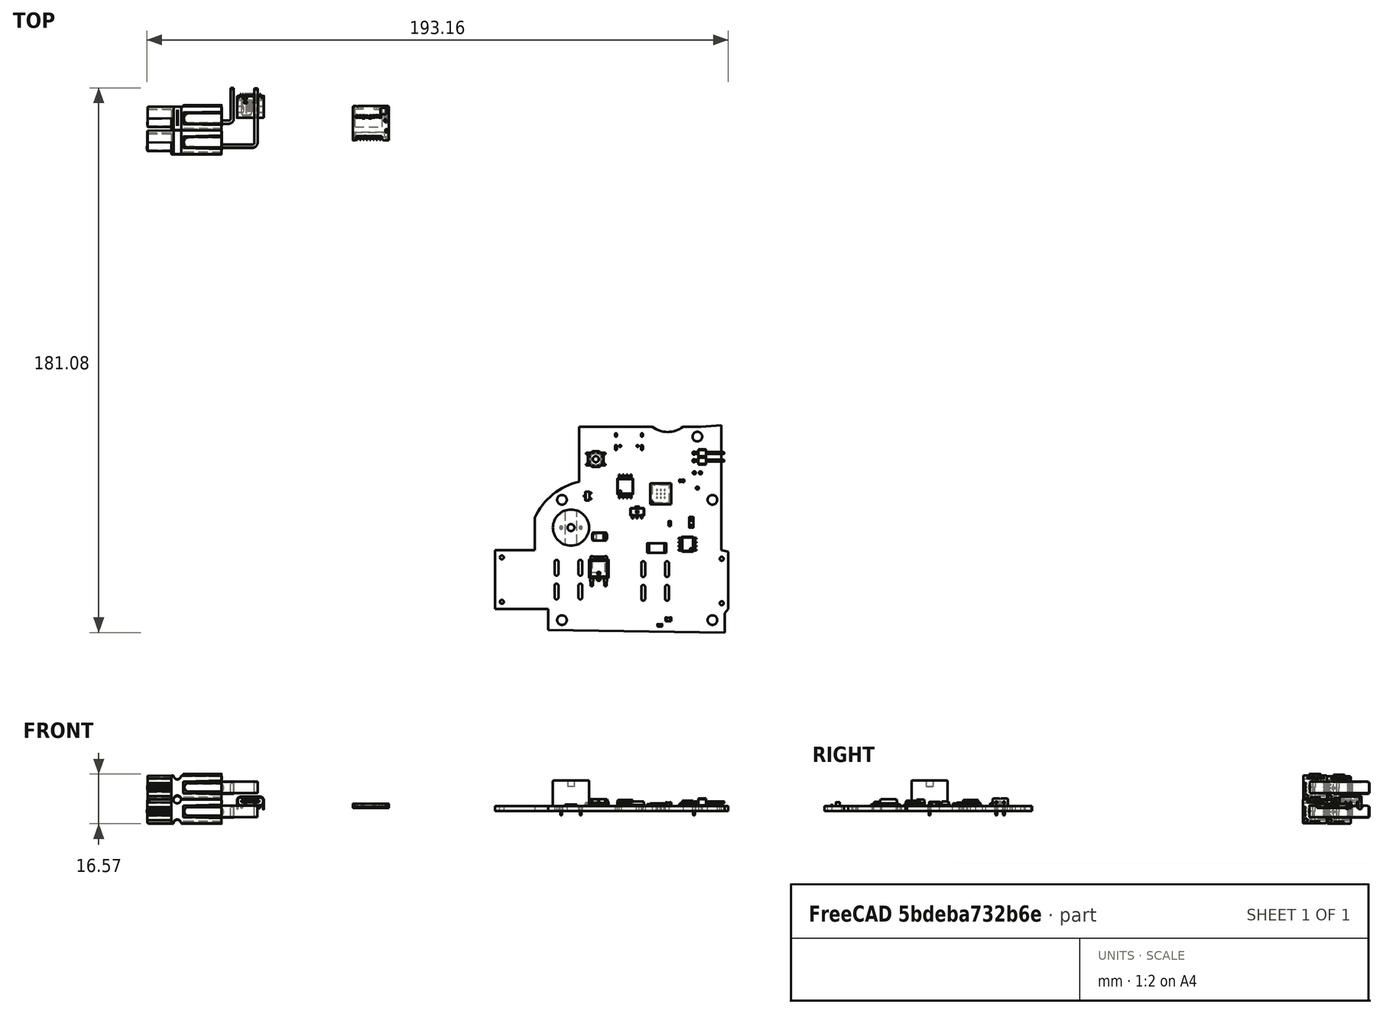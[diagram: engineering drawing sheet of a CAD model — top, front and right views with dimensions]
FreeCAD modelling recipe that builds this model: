
FCSTD DOCUMENT  (FreeCAD 0.20R27537 (Git))
Label: board
License: All rights reserved
LicenseURL: http://en.wikipedia.org/wiki/All_rights_reserved
objects: App::Link×56, Part::Feature×38, App::Part×8, PartDesign::CoordinateSystem×1, Sketcher::SketchObject×1
note: 40 computed .brp shape members not serialized (recipe doc carries the construction recipe); baked Part::Feature solids carry a one-line shape summary decoded from their .brp

FEATURE [PartDesign::CoordinateSystem] Local_CS_a133
  AttacherType = Attacher::AttachEngine3D
FEATURE [Part::Feature] Pcb_a133
  shape: bbox 77.5 x 68.95 x 1.6 mm, 118 faces (baked)
FEATURE [Sketcher::SketchObject] PCB_Sketch_a133
  ExternalGeometry = -> [Pcb_a133]
  FullyConstrained = false
  sketch-geometry (42):
    g0: ArcOfCircle CenterX=143.125 CenterY=-95.9167 CenterZ=0 NormalX=0 NormalY=0 NormalZ=-1 AngleXU=-2.2143 Radius=8.54167 StartAngle=0 EndAngle=1.287
    g1: LineSegment StartX=100.518 StartY=-132.657 StartZ=0 EndX=100.518 EndY=-140.91 EndZ=0
    g2: LineSegment StartX=97.2675 StartY=-144.16 StartZ=0 EndX=89.2675 EndY=-144.16 EndZ=0
    g3: LineSegment StartX=86.0175 StartY=-147.41 StartZ=0 EndX=86.0175 EndY=-159.69 EndZ=0
    g4: LineSegment StartX=89.2675 StartY=-162.94 StartZ=0 EndX=100.75 EndY=-162.94 EndZ=0
    g5: LineSegment StartX=104 StartY=-166.19 StartZ=0 EndX=104 EndY=-167.75 EndZ=0
    g6: LineSegment StartX=107.25 StartY=-171 StartZ=0 EndX=159.85 EndY=-171 EndZ=0
    g7: LineSegment StartX=163.1 StartY=-167.75 StartZ=0 EndX=163.1 EndY=-166.75 EndZ=0
    g8: LineSegment StartX=163.1 StartY=-166.75 StartZ=0 EndX=163.1 EndY=-146.61 EndZ=0
    g9: LineSegment StartX=161.1 StartY=-144.61 StartZ=0 EndX=160.25 EndY=-144.61 EndZ=0
    g10: LineSegment StartX=157 StartY=-141.36 StartZ=0 EndX=157 EndY=-132 EndZ=0
    g11: ArcOfCircle CenterX=158 CenterY=-127 CenterZ=0 NormalX=0 NormalY=0 NormalZ=1 AngleXU=0 Radius=4 StartAngle=4.71239 EndAngle=7.85398
    g12: LineSegment StartX=157 StartY=-122 StartZ=0 EndX=157 EndY=-106 EndZ=0
    g13: LineSegment StartX=153.75 StartY=-102.75 StartZ=0 EndX=148.25 EndY=-102.75 EndZ=0
    g14: LineSegment StartX=138 StartY=-102.75 StartZ=0 EndX=116.25 EndY=-102.75 EndZ=0
    g15: LineSegment StartX=113 StartY=-106 StartZ=0 EndX=113 EndY=-117.5 EndZ=0
    g16: ArcOfCircle CenterX=112.711 CenterY=-132.657 CenterZ=0 NormalX=0 NormalY=0 NormalZ=1 AngleXU=0 Radius=12.1931 StartAngle=1.7637 EndAngle=3.14159
    g17: GeomPoint X=106.689 Y=-126.083 Z=0
    g18: GeomPoint X=102.635 Y=-125.79 Z=0
    g19: ArcOfCircle CenterX=158 CenterY=-132 CenterZ=0 NormalX=0 NormalY=0 NormalZ=1 AngleXU=0 Radius=1 StartAngle=1.5708 EndAngle=3.14159
    g20: ArcOfCircle CenterX=160.25 CenterY=-141.36 CenterZ=0 NormalX=0 NormalY=0 NormalZ=1 AngleXU=0 Radius=3.25 StartAngle=3.14159 EndAngle=4.71239
    g21: GeomPoint X=157 Y=-144.61 Z=0
    g22: ArcOfCircle CenterX=161.1 CenterY=-146.61 CenterZ=0 NormalX=0 NormalY=0 NormalZ=1 AngleXU=0 Radius=2 StartAngle=-2.7e-15 EndAngle=1.5708
    g23: GeomPoint X=163.1 Y=-144.61 Z=0
    g24: ArcOfCircle CenterX=158 CenterY=-122 CenterZ=0 NormalX=0 NormalY=0 NormalZ=1 AngleXU=0 Radius=1 StartAngle=3.14159 EndAngle=4.71239
    g25: ArcOfCircle CenterX=153.75 CenterY=-106 CenterZ=0 NormalX=0 NormalY=0 NormalZ=1 AngleXU=0 Radius=3.25 StartAngle=1.3e-15 EndAngle=1.5708
    g26: GeomPoint X=157 Y=-102.75 Z=0
    g27: ArcOfCircle CenterX=116.25 CenterY=-106 CenterZ=0 NormalX=0 NormalY=0 NormalZ=1 AngleXU=0 Radius=3.25 StartAngle=1.5708 EndAngle=3.14159
    g28: GeomPoint X=113 Y=-102.75 Z=0
    g29: ArcOfCircle CenterX=109.75 CenterY=-117.5 CenterZ=0 NormalX=0 NormalY=0 NormalZ=1 AngleXU=0 Radius=3.25 StartAngle=4.90529 EndAngle=6.28319
    g30: ArcOfCircle CenterX=97.2675 CenterY=-140.91 CenterZ=0 NormalX=0 NormalY=0 NormalZ=1 AngleXU=0 Radius=3.25 StartAngle=4.71239 EndAngle=6.28319
    g31: GeomPoint X=100.518 Y=-144.16 Z=0
    g32: ArcOfCircle CenterX=89.2675 CenterY=-147.41 CenterZ=0 NormalX=0 NormalY=0 NormalZ=1 AngleXU=0 Radius=3.25 StartAngle=1.5708 EndAngle=3.14159
    g33: GeomPoint X=86.0175 Y=-144.16 Z=0
    g34: ArcOfCircle CenterX=89.2675 CenterY=-159.69 CenterZ=0 NormalX=0 NormalY=0 NormalZ=1 AngleXU=0 Radius=3.25 StartAngle=3.14159 EndAngle=4.71239
    g35: GeomPoint X=86.0175 Y=-162.94 Z=0
    g36: ArcOfCircle CenterX=100.75 CenterY=-166.19 CenterZ=0 NormalX=0 NormalY=0 NormalZ=1 AngleXU=0 Radius=3.25 StartAngle=-2.7e-15 EndAngle=1.5708
    g37: GeomPoint X=104 Y=-162.94 Z=0
    g38: ArcOfCircle CenterX=107.25 CenterY=-167.75 CenterZ=0 NormalX=0 NormalY=0 NormalZ=1 AngleXU=0 Radius=3.25 StartAngle=3.14159 EndAngle=4.71239
    g39: GeomPoint X=104 Y=-171 Z=0
    g40: ArcOfCircle CenterX=159.85 CenterY=-167.75 CenterZ=0 NormalX=0 NormalY=0 NormalZ=1 AngleXU=0 Radius=3.25 StartAngle=4.71239 EndAngle=6.28319
    g41: GeomPoint X=163.1 Y=-171 Z=0
  constraints (102):
    c: DistanceX(g-6,g-5) = 50
    c: DistanceX(g-3,g-4) = 50
    c: DistanceY(g-4,g-5) = 40
    c: DistanceY(g-3,g-6) = 40
    c: DistanceY(g-5,g-7) = 21
    c: DistanceX(g-7,g-5) = 5
    c: Horizontal(g2)
    c: Vertical(g3)
    c: Horizontal(g4)
    c: Vertical(g5)
    c: Horizontal(g6)
    c: Vertical(g7)
    c: Vertical(g8)
    c: Horizontal(g9)
    c: Vertical(g10)
    c: Coincident(g11,g-5)
    c: Coincident(g13,g0)
    c: Coincident(g14,g0)
    c: Horizontal(g14)
    c: Vertical(g15)
    c: Coincident(g16,g1)
    c: Vertical(g12)
    c: Horizontal(g13)
    c: Equal(g0,g-12)
    c: Coincident(g0,g-12)
    c: Coincident(g0,g-12)
    c: DistanceX(g-7,g26) = 4
    c: DistanceX(g-8,g23) = 2
    c: DistanceX(g33,g-10) = 2
    c: DistanceX(g39,g-3) = 4
    c: DistanceY(g39,g-3) = 4
    c: DistanceY(g-8,g23) = 2
    c: DistanceY(g35,g-11) = 2
    c: DistanceY(g-10,g33) = 2
    c: DistanceX(g28,g14) = 25
    c: PointOnObject(g17,g-6)
    c: PointOnObject(g18,g16)
    c: Distance(g-6,g18) = 5.5
    c: Tangent(g11,g19) = 1.5708
    c: Tangent(g10,g19) = 1.5708
    c: PointOnObject(g21,g10)
    c: PointOnObject(g21,g9)
    c: Tangent(g10,g20) = 1.5708
    c: Tangent(g9,g20) = 1.5708
    c: PointOnObject(g23,g9)
    c: PointOnObject(g23,g8)
    c: Tangent(g9,g22) = -1.5708
    c: Tangent(g8,g22) = -1.5708
    c: Tangent(g11,g24) = 1.5708
    c: Tangent(g12,g24) = 1.5708
    c: PointOnObject(g26,g12)
    c: PointOnObject(g26,g13)
    c: Tangent(g12,g25) = -1.5708
    c: Tangent(g13,g25) = -1.5708
    c: PointOnObject(g28,g14)
    c: PointOnObject(g28,g15)
    c: Tangent(g14,g27) = -1.5708
    c: Tangent(g15,g27) = -1.5708
    c: Tangent(g16,g29) = 1.5708
    c: Tangent(g15,g29) = 1.5708
    c: PointOnObject(g31,g2)
    c: PointOnObject(g31,g1)
    c: Tangent(g2,g30) = 1.5708
    c: Tangent(g1,g30) = 1.5708
    c: PointOnObject(g33,g3)
    c: PointOnObject(g33,g2)
    c: Tangent(g3,g32) = -1.5708
    c: Tangent(g2,g32) = -1.5708
    c: PointOnObject(g35,g3)
    c: PointOnObject(g35,g4)
    c: Tangent(g3,g34) = -1.5708
    c: Tangent(g4,g34) = -1.5708
    c: PointOnObject(g37,g5)
    c: PointOnObject(g37,g4)
    c: Tangent(g5,g36) = 1.5708
    c: Tangent(g4,g36) = 1.5708
    c: PointOnObject(g39,g5)
    c: PointOnObject(g39,g6)
    c: Tangent(g5,g38) = -1.5708
    c: Tangent(g6,g38) = -1.5708
    c: PointOnObject(g41,g6)
    c: PointOnObject(g41,g7)
    c: Tangent(g6,g40) = -1.5708
    c: Tangent(g7,g40) = -1.5708
    c: Coincident(g7,g8)
    c: Equal(g40,g38)
    c: Equal(g36,g34)
    c: Equal(g32,g34)
    c: Equal(g30,g32)
    c: Equal(g30,g20)
    c: Equal(g19,g24)
    c: Equal(g25,g27)
    c: Equal(g27,g29)
    c: Equal(g27,g30)
    c: Equal(g40,g25)
    c: Vertical(g10,g12)
    c: Radius(g11) = 4
    c: Vertical(g11,g24)
    c: Horizontal(g22,g-8)
    c: DistanceY(g7,g7) = 1
    c: DistanceY(g15,g15) = 11.5
    c: Block(g1)
FEATURE [App::Part] Board_Geoms_a133
  Group = -> [Local_CS_a133,Pcb_a133,PCB_Sketch_a133]
  Origin = -> Origin
FEATURE [Part::Feature] Shape  label="C11_C_0603_1608Metric_b2591ca4353f"
  Placement = pos=(147.8,-120.7,0) rot=(0,0,1;0rad)
  shape: bbox 1.6 x 0.8 x 0.8 mm, 28 faces (baked)
FEATURE [Part::Feature] Shape001  label="U4_SOIC_8_39x49mm_P127mm_40db203ede0f"
  Placement = pos=(149.75,-141.75,0) rot=(0,0,1;3.14159rad)
  shape: bbox 6 x 4.9 x 1.75 mm, 156 faces (baked)
FEATURE [Part::Feature] Shape002  label="R11_R_0603_1608Metric_8d44d50ded66"
  Placement = pos=(140.5,-168.75,0) rot=(0,0,1;3.14159rad)
  shape: bbox 1.6 x 0.8 x 0.45 mm, 26 faces (baked)
FEATURE [App::Link] C11_C_0603_1608Metric_b2591ca4353f_ln_  label="C1_C_0603_1608Metric_4f53b00ce3c0"
  LinkPlacement = pos=(132.368,-165.3,0) rot=(0,0,-1;1.5708rad)
  LinkedObject = -> Shape
  Placement = pos=(132.368,-165.3,0) rot=(0,0,-1;1.5708rad)
FEATURE [App::Link] C11_C_0603_1608Metric_b2591ca4353f_ln_001  label="C22_C_0603_1608Metric_e7c7fc5a71bd"
  LinkPlacement = pos=(138,-131.31,0) rot=(0,0,-1;1.5708rad)
  LinkedObject = -> Shape
  Placement = pos=(138,-131.31,0) rot=(0,0,-1;1.5708rad)
FEATURE [App::Link] R11_R_0603_1608Metric_8d44d50ded66_ln_  label="R18_R_0603_1608Metric_e3e5b9e3ae07"
  LinkPlacement = pos=(134.5,-122.35,0) rot=(0,0,1;3.14159rad)
  LinkedObject = -> Shape002
  Placement = pos=(134.5,-122.35,0) rot=(0,0,1;3.14159rad)
FEATURE [Part::Feature] Shape003  label="U2_SOT_89_3_d67087812165"
  Placement = pos=(133,-131.25,0) rot=(0,0,1;1.5708rad)
  shape: bbox 4.5 x 4 x 1.52 mm, 43 faces (baked)
FEATURE [App::Link] R11_R_0603_1608Metric_8d44d50ded66_ln_001  label="R29_R_0603_1608Metric_036824cd240c"
  LinkPlacement = pos=(148.25,-136.25,0) rot=(0,0,1;0rad)
  LinkedObject = -> Shape002
  Placement = pos=(148.25,-136.25,0) rot=(0,0,1;0rad)
FEATURE [App::Link] R11_R_0603_1608Metric_8d44d50ded66_ln_002  label="R15_R_0603_1608Metric_e011a92e6b2f"
  LinkPlacement = pos=(150,-117,0) rot=(0,0,1;1.5708rad)
  LinkedObject = -> Shape002
  Placement = pos=(150,-117,0) rot=(0,0,1;1.5708rad)
FEATURE [Part::Feature] Part__Feature  label="ConPins"
  shape: bbox 6 x 4.32 x 0.61 mm, 70 faces (baked)
FEATURE [Part::Feature] Part__Feature001  label="PcbPins"
  shape: bbox 6.9 x 0.99 x 0.3 mm, 122 faces (baked)
FEATURE [Part::Feature] Part__Feature002  label="Mold"
  shape: bbox 8.95 x 6.5 x 3.731 mm, 55 faces (baked)
FEATURE [Part::Feature] Part__Feature003  label="Frame"
  shape: bbox 8.95 x 7.3 x 4.2 mm, 323 faces (baked)
FEATURE [App::Part] HRO_TYPE_C_31_M_12  label="J5_HRO_TYPE_C_31_M_12_ee36a14f041e"
  Group = -> [Part__Feature,Part__Feature001,Part__Feature002,Part__Feature003]
  Origin = -> Origin008
  Placement = pos=(134.75,-103,0) rot=(0,0,1;3.14159rad)
FEATURE [App::Link] C11_C_0603_1608Metric_b2591ca4353f_ln_002  label="C14_C_0603_1608Metric_768d27e505bd"
  LinkPlacement = pos=(137.75,-119.15,0) rot=(0,0,1;0rad)
  LinkedObject = -> Shape
  Placement = pos=(137.75,-119.15,0) rot=(0,0,1;0rad)
FEATURE [App::Link] R11_R_0603_1608Metric_8d44d50ded66_ln_003  label="R17_R_0603_1608Metric_fb0f977e1867"
  LinkPlacement = pos=(145.5,-130.81,0) rot=(0,0,1;1.5708rad)
  LinkedObject = -> Shape002
  Placement = pos=(145.5,-130.81,0) rot=(0,0,1;1.5708rad)
FEATURE [App::Link] U2_SOT_89_3_d67087812165_ln_  label="U6_SOT_89_3_2ae91e355754"
  LinkPlacement = pos=(127.5,-131.25,0) rot=(0,0,1;1.5708rad)
  LinkedObject = -> Shape003
  Placement = pos=(127.5,-131.25,0) rot=(0,0,1;1.5708rad)
FEATURE [App::Link] C11_C_0603_1608Metric_b2591ca4353f_ln_003  label="C6_C_0603_1608Metric_0048e40f4021"
  LinkPlacement = pos=(125,-119.56,0) rot=(0,0,-1;1.5708rad)
  LinkedObject = -> Shape
  Placement = pos=(125,-119.56,0) rot=(0,0,-1;1.5708rad)
FEATURE [Part::Feature] Part__Feature004  label="SOLID"
  shape: bbox 11.95 x 11.4 x 1.451 mm, 410 faces (baked)
FEATURE [App::Part] _040310811  label="J2_1040310811_9c2815c498c7[2]"
  Group = -> [Part__Feature004]
  Origin = -> Origin009
  Placement = pos=(187.5,-113.81,0.5) rot=(0,0,1;3.14159rad)
FEATURE [Part::Feature] Part__Feature005  label="_14555P6"
  Placement = pos=(-20,7.5,9) rot=(0.707107,0,-0.707107;3.14159rad)
  shape: bbox 1 x 1.5 x 1.5 mm, 1 faces, 0 solids (baked)
FEATURE [Part::Feature] Part__Feature006  label="_14555P007"
  Placement = pos=(-20,7.5,9) rot=(0.707107,0,-0.707107;3.14159rad)
  shape: bbox 1 x 1.5 x 1.5 mm, 1 faces, 0 solids (baked)
FEATURE [Part::Feature] Part__Feature007  label="_14555P008"
  Placement = pos=(-20,7.5,9) rot=(0.707107,0,-0.707107;3.14159rad)
  shape: bbox 1 x 19.5 x 0.5 mm, 1 faces, 0 solids (baked)
FEATURE [Part::Feature] Part__Feature008  label="_14555P009"
  Placement = pos=(-20,7.5,9) rot=(0.707107,0,-0.707107;3.14159rad)
  shape: bbox 1 x 0.5 x 12.5 mm, 1 faces, 0 solids (baked)
FEATURE [Part::Feature] Part__Feature009  label="_14555P010"
  Placement = pos=(-20,7.5,9) rot=(0.707107,0,-0.707107;3.14159rad)
  shape: bbox 1 x 19.5 x 0.5 mm, 1 faces, 0 solids (baked)
FEATURE [Part::Feature] Part__Feature010  label="_14555P011"
  Placement = pos=(-20,7.5,9) rot=(0.707107,0,-0.707107;3.14159rad)
  shape: bbox 1 x 19.5 x 0.5 mm, 1 faces, 0 solids (baked)
FEATURE [Part::Feature] Part__Feature011  label="_14555P012"
  Placement = pos=(-20,7.5,9) rot=(0.707107,0,-0.707107;3.14159rad)
  shape: bbox 1 x 1.5 x 1.5 mm, 1 faces, 0 solids (baked)
FEATURE [Part::Feature] Part__Feature012  label="_14555P013"
  Placement = pos=(-20,7.5,9) rot=(0.707107,0,-0.707107;3.14159rad)
  shape: bbox 1 x 0.5 x 12.5 mm, 1 faces, 0 solids (baked)
FEATURE [Part::Feature] Part__Feature013  label="_14555P014"
  Placement = pos=(-20,7.5,9) rot=(0.707107,0,-0.707107;3.14159rad)
  shape: bbox 1 x 1.5 x 1.5 mm, 1 faces, 0 solids (baked)
FEATURE [Part::Feature] Part__Feature014  label="_14555P015"
  Placement = pos=(-20,7.5,9) rot=(0.707107,0,-0.707107;3.14159rad)
  shape: bbox 1 x 19.5 x 0.5 mm, 1 faces, 0 solids (baked)
FEATURE [Part::Feature] Part__Feature015  label="_14555P016"
  Placement = pos=(-20,7.5,9) rot=(0.707107,0,-0.707107;3.14159rad)
  shape: bbox 1.012 x 2e-07 x 1.012 mm, 1 faces, 0 solids (baked)
FEATURE [Part::Feature] Part__Feature016  label="_14555P017"
  Placement = pos=(-20,7.5,9) rot=(0.707107,0,-0.707107;3.14159rad)
  shape: bbox 1.012 x 2e-07 x 1.012 mm, 1 faces, 0 solids (baked)
FEATURE [App::Part] _14555P6  label="_14555P018"
  Group = -> [Part__Feature005,Part__Feature006,Part__Feature007,Part__Feature008,Part__Feature009,Part__Feature010,Part__Feature011,Part__Feature012,Part__Feature013,Part__Feature014,Part__Feature015,Part__Feature016]
  Origin = -> Origin010
FEATURE [Part::Feature] Part__Feature017  label="1336G1 IN HSG"
  shape: bbox 28.76 x 14.07 x 8.413 mm, 345 faces (baked)
FEATURE [Part::Feature] Part__Feature018  label="1337G1 IN HSG"
  Placement = pos=(-5.19151,38.6216,45.5) rot=(0.707107,0,0.707107;3.14159rad)
  shape: bbox 36.7 x 21.92 x 8.407 mm, 344 faces (baked)
FEATURE [Part::Feature] Part__Feature019  label="1336G1 IN HSG001"
  Placement = pos=(0,0,7.875) rot=(0,0,1;0rad)
  shape: bbox 28.76 x 14.07 x 8.413 mm, 345 faces (baked)
FEATURE [Part::Feature] Part__Feature020  label="1337G1 IN HSG001"
  Placement = pos=(-5.12833,38.7239,53.5) rot=(0.707107,0,0.707107;3.14159rad)
  shape: bbox 36.7 x 21.92 x 8.407 mm, 344 faces (baked)
FEATURE [App::Part] _x2PP  label="J1__x2PP_7d6c331e9d58"
  Group = -> [_14555P6,Part__Feature017,Part__Feature018,Part__Feature019,Part__Feature020]
  Origin = -> Origin011
  Placement = pos=(107.618,-155.55,4.5) rot=(-1,0,0;1.5708rad)
FEATURE [App::Link] C11_C_0603_1608Metric_b2591ca4353f_ln_004  label="C10_C_0603_1608Metric_d6ead46ee743"
  LinkPlacement = pos=(151.25,-126.06,0) rot=(0,0,-1;1.5708rad)
  LinkedObject = -> Shape
  Placement = pos=(151.25,-126.06,0) rot=(0,0,-1;1.5708rad)
FEATURE [Part::Feature] Shape004  label="Q6_TO_252_2_4d53b22412b7"
  Placement = pos=(120.225,-150.775,0) rot=(0,0,1;1.5708rad)
  shape: bbox 6.5 x 9.9 x 2.32 mm, 80 faces (baked)
FEATURE [App::Link] R11_R_0603_1608Metric_8d44d50ded66_ln_004  label="R10_R_0603_1608Metric_e035e099a75d"
  LinkPlacement = pos=(119.5,-125.75,0) rot=(0,0,-1;1.5708rad)
  LinkedObject = -> Shape002
  Placement = pos=(119.5,-125.75,0) rot=(0,0,-1;1.5708rad)
FEATURE [App::Link] C11_C_0603_1608Metric_b2591ca4353f_ln_005  label="C3_C_0603_1608Metric_5b8c0d85cd26"
  LinkPlacement = pos=(131.75,-135.25,0) rot=(0,0,1;3.14159rad)
  LinkedObject = -> Shape
  Placement = pos=(131.75,-135.25,0) rot=(0,0,1;3.14159rad)
FEATURE [Part::Feature] Shape005  label="BZ1_MagneticBuzzer_ProSignal_ABT_410_RC_121c1aeb4457"
  Placement = pos=(107.75,-136.25,0) rot=(0,0,1;0rad)
  shape: bbox 12.99 x 12.99 x 11.53 mm, 19 faces (baked)
FEATURE [Part::Feature] Shape006  label="C2_C_0805_2012Metric_9981c835235c"
  Placement = pos=(143.368,-166.75,0) rot=(0,0,1;3.14159rad)
  shape: bbox 2 x 1.25 x 1.25 mm, 28 faces (baked)
FEATURE [Part::Feature] Shape007  label="D1_D_SMA_ee7b9d5fba9a"
  Placement = pos=(120.5,-139.25,0) rot=(0,0,1;3.14159rad)
  shape: bbox 5 x 2.7 x 2.22 mm, 41 faces (baked)
FEATURE [Part::Feature] Shape008  label="D13_D_MiniMELF_Standard_9158ad23d143"
  Placement = pos=(151,-134.5,0) rot=(0,0,-1;1.5708rad)
  shape: bbox 1.4 x 3.6 x 1.4 mm, 13 faces (baked)
FEATURE [App::Link] R11_R_0603_1608Metric_8d44d50ded66_ln_005  label="R22_R_0603_1608Metric_0d59d87862aa"
  LinkPlacement = pos=(142.05,-134.95,0) rot=(0,0,1;1.5708rad)
  LinkedObject = -> Shape002
  Placement = pos=(142.05,-134.95,0) rot=(0,0,1;1.5708rad)
FEATURE [App::Link] R11_R_0603_1608Metric_8d44d50ded66_ln_006  label="R23_R_0603_1608Metric_380181a35113"
  LinkPlacement = pos=(151.5,-138,0) rot=(0,0,1;0rad)
  LinkedObject = -> Shape002
  Placement = pos=(151.5,-138,0) rot=(0,0,1;0rad)
FEATURE [App::Link] D13_D_MiniMELF_Standard_9158ad23d143_ln_  label="D12_D_MiniMELF_Standard_02d884a8e2a8"
  LinkPlacement = pos=(117.5,-129.75,0) rot=(0,0,1;3.14159rad)
  LinkedObject = -> Shape008
  Placement = pos=(117.5,-129.75,0) rot=(0,0,1;3.14159rad)
FEATURE [App::Link] C11_C_0603_1608Metric_b2591ca4353f_ln_006  label="C21_C_0603_1608Metric_2dd047efe488"
  LinkPlacement = pos=(143.6,-131.675,0) rot=(0,0,-1;1.5708rad)
  LinkedObject = -> Shape
  Placement = pos=(143.6,-131.675,0) rot=(0,0,-1;1.5708rad)
FEATURE [App::Link] C11_C_0603_1608Metric_b2591ca4353f_ln_007  label="C12_C_0603_1608Metric_b0e708ee7b5c"
  LinkPlacement = pos=(134.5,-119.25,0) rot=(0,0,1;3.14159rad)
  LinkedObject = -> Shape
  Placement = pos=(134.5,-119.25,0) rot=(0,0,1;3.14159rad)
FEATURE [App::Link] C11_C_0603_1608Metric_b2591ca4353f_ln_008  label="C15_C_0603_1608Metric_9958e1d70984"
  LinkPlacement = pos=(134.5,-117.7,0) rot=(0,0,1;3.14159rad)
  LinkedObject = -> Shape
  Placement = pos=(134.5,-117.7,0) rot=(0,0,1;3.14159rad)
FEATURE [App::Link] C11_C_0603_1608Metric_b2591ca4353f_ln_009  label="C16_C_0603_1608Metric_8f8f7e44dc67"
  LinkPlacement = pos=(125.725,-135.25,0) rot=(0,0,1;3.14159rad)
  LinkedObject = -> Shape
  Placement = pos=(125.725,-135.25,0) rot=(0,0,1;3.14159rad)
FEATURE [App::Link] C11_C_0603_1608Metric_b2591ca4353f_ln_010  label="C13_C_0603_1608Metric_fae38cec52d1"
  LinkPlacement = pos=(143.025,-119.56,0) rot=(0,0,1;0rad)
  LinkedObject = -> Shape
  Placement = pos=(143.025,-119.56,0) rot=(0,0,1;0rad)
FEATURE [Part::Feature] Shape009  label="TH1_PinHeader_1x02_P254mm_Horizontal_3983d4666e7b"
  Placement = pos=(151.875,-111.475,0) rot=(0,0,1;0rad)
  shape: bbox 10.36 x 5.08 x 5.54 mm, 58 faces (baked)
FEATURE [Part::Feature] Shape010  label="Q7_SOT_23_3ce7cc26b8bc"
  Placement = pos=(116.5,-125.75,0) rot=(0,0,1;3.14159rad)
  shape: bbox 2.5 x 3 x 1.2 mm, 76 faces (baked)
FEATURE [App::Link] D1_D_SMA_ee7b9d5fba9a_ln_  label="D8_D_SMA_7948d8de446f"
  LinkPlacement = pos=(139,-154,0) rot=(0,0,-1;1.5708rad)
  LinkedObject = -> Shape007
  Placement = pos=(139,-154,0) rot=(0,0,-1;1.5708rad)
FEATURE [App::Link] C11_C_0603_1608Metric_b2591ca4353f_ln_011  label="C5_C_0603_1608Metric_6f59efa6d383"
  LinkPlacement = pos=(134.25,-114.25,0) rot=(0,0,1;0rad)
  LinkedObject = -> Shape
  Placement = pos=(134.25,-114.25,0) rot=(0,0,1;0rad)
FEATURE [App::Link] J1__x2PP_7d6c331e9d58_ln_  label="J4__x2PP_4cc251a55201"
  LinkPlacement = pos=(141.5,-152,4.5) rot=(0,-0.707107,0.707107;3.14159rad)
  LinkedObject = -> _x2PP
  Placement = pos=(141.5,-152,4.5) rot=(0,-0.707107,0.707107;3.14159rad)
FEATURE [App::Link] R11_R_0603_1608Metric_8d44d50ded66_ln_007  label="R13_R_0603_1608Metric_4da9fd97616e"
  LinkPlacement = pos=(125,-116,0) rot=(0,0,-1;1.5708rad)
  LinkedObject = -> Shape002
  Placement = pos=(125,-116,0) rot=(0,0,-1;1.5708rad)
FEATURE [App::Link] Q6_TO_252_2_4d53b22412b7_ln_  label="Q3_TO_252_2_50c79828837a"
  LinkPlacement = pos=(120,-164.25,0) rot=(0,0,-1;1.5708rad)
  LinkedObject = -> Shape004
  Placement = pos=(120,-164.25,0) rot=(0,0,-1;1.5708rad)
FEATURE [Part::Feature] Shape011  label="SW4_SW_SPST_TL3342_7108015214c8"
  Placement = pos=(119.25,-113.5,0) rot=(0,0,1;3.14159rad)
  shape: bbox 6.401 x 5.201 x 1.541 mm, 193 faces (baked)
FEATURE [App::Link] SW4_SW_SPST_TL3342_7108015214c8_ln_  label="SW3_SW_SPST_TL3342_df33c48a9ac6"
  LinkPlacement = pos=(119.25,-120,0) rot=(0,0,1;3.14159rad)
  LinkedObject = -> Shape011
  Placement = pos=(119.25,-120,0) rot=(0,0,1;3.14159rad)
FEATURE [App::Link] R11_R_0603_1608Metric_8d44d50ded66_ln_008  label="R12_R_0603_1608Metric_07ab9bbcb2c5"
  LinkPlacement = pos=(134,-168.75,0) rot=(0,0,1;0rad)
  LinkedObject = -> Shape002
  Placement = pos=(134,-168.75,0) rot=(0,0,1;0rad)
FEATURE [App::Link] D1_D_SMA_ee7b9d5fba9a_ln_001  label="D10_D_SMA_68e82023299a"
  LinkPlacement = pos=(122.25,-126.75,0) rot=(0,0,1;1.5708rad)
  LinkedObject = -> Shape007
  Placement = pos=(122.25,-126.75,0) rot=(0,0,1;1.5708rad)
FEATURE [Part::Feature] Shape012  label="D9_LED_0603_1608Metric_691726ff2c38"
  Placement = pos=(143.8,-134.95,0) rot=(0,0,1;1.5708rad)
  shape: bbox 0.8 x 1.6 x 1.1 mm, 50 faces (baked)
FEATURE [App::Link] C11_C_0603_1608Metric_b2591ca4353f_ln_012  label="C4_C_0603_1608Metric_5b89fb0e1c07"
  LinkPlacement = pos=(134.75,-135.25,0) rot=(0,0,1;3.14159rad)
  LinkedObject = -> Shape
  Placement = pos=(134.75,-135.25,0) rot=(0,0,1;3.14159rad)
FEATURE [App::Link] D1_D_SMA_ee7b9d5fba9a_ln_002  label="D3_D_SMA_e5673b74acae"
  LinkPlacement = pos=(120.5,-143,0) rot=(0,0,1;3.14159rad)
  LinkedObject = -> Shape007
  Placement = pos=(120.5,-143,0) rot=(0,0,1;3.14159rad)
FEATURE [App::Link] R11_R_0603_1608Metric_8d44d50ded66_ln_009  label="R27_R_0603_1608Metric_2b64b2a65876"
  LinkPlacement = pos=(118,-132.5,0) rot=(0,0,1;0rad)
  LinkedObject = -> Shape002
  Placement = pos=(118,-132.5,0) rot=(0,0,1;0rad)
FEATURE [App::Link] R11_R_0603_1608Metric_8d44d50ded66_ln_010  label="R20_R_0603_1608Metric_7287fd6f59e4"
  LinkPlacement = pos=(127.425,-113.06,0) rot=(0,0,1;0rad)
  LinkedObject = -> Shape002
  Placement = pos=(127.425,-113.06,0) rot=(0,0,1;0rad)
FEATURE [App::Link] C11_C_0603_1608Metric_b2591ca4353f_ln_013  label="C8_C_0603_1608Metric_686d20fc0d8d"
  LinkPlacement = pos=(148.25,-138,0) rot=(0,0,1;0rad)
  LinkedObject = -> Shape
  Placement = pos=(148.25,-138,0) rot=(0,0,1;0rad)
FEATURE [Part::Feature] Shape013  label="U5_QFN-56-1EP_7x7mm_Pitch0.4mm_28ac528c9c57"
  Placement = pos=(140.85,-125.01,0) rot=(0,0,1;1.5708rad)
  shape: bbox 7 x 7 x 0.92 mm, 350 faces (baked)
FEATURE [App::Link] Q6_TO_252_2_4d53b22412b7_ln_001  label="Q2_TO_252_2_cf809253fdf2"
  LinkPlacement = pos=(127.475,-164.175,0) rot=(0,0,-1;1.5708rad)
  LinkedObject = -> Shape004
  Placement = pos=(127.475,-164.175,0) rot=(0,0,-1;1.5708rad)
FEATURE [App::Link] SW4_SW_SPST_TL3342_7108015214c8_ln_001  label="SW1_SW_SPST_TL3342_a0f9d60d01a4"
  LinkPlacement = pos=(149.618,-165.8,0) rot=(0,0,1;0rad)
  LinkedObject = -> Shape011
  Placement = pos=(149.618,-165.8,0) rot=(0,0,1;0rad)
FEATURE [App::Link] C11_C_0603_1608Metric_b2591ca4353f_ln_014  label="C20_C_0603_1608Metric_ecb0d8d6a8ff"
  LinkPlacement = pos=(142,-131.7,0) rot=(0,0,-1;1.5708rad)
  LinkedObject = -> Shape
  Placement = pos=(142,-131.7,0) rot=(0,0,-1;1.5708rad)
FEATURE [App::Link] Q6_TO_252_2_4d53b22412b7_ln_002  label="Q5_TO_252_2_8872d78e0328"
  LinkPlacement = pos=(127.725,-150.775,0) rot=(0,0,1;1.5708rad)
  LinkedObject = -> Shape004
  Placement = pos=(127.725,-150.775,0) rot=(0,0,1;1.5708rad)
FEATURE [App::Link] C11_C_0603_1608Metric_b2591ca4353f_ln_015  label="C19_C_0603_1608Metric_04f3e79b6c38"
  LinkPlacement = pos=(128.775,-135.25,0) rot=(0,0,1;3.14159rad)
  LinkedObject = -> Shape
  Placement = pos=(128.775,-135.25,0) rot=(0,0,1;3.14159rad)
FEATURE [App::Link] R11_R_0603_1608Metric_8d44d50ded66_ln_011  label="R1_R_0603_1608Metric_4082b09b0587"
  LinkPlacement = pos=(143.368,-164.5,0) rot=(0,0,1;3.14159rad)
  LinkedObject = -> Shape002
  Placement = pos=(143.368,-164.5,0) rot=(0,0,1;3.14159rad)
FEATURE [Part::Feature] Shape014  label="R14_R_2512_6332Metric_da6ad8455e88"
  Placement = pos=(139.5,-143,0) rot=(0,0,1;0rad)
  shape: bbox 6.3 x 3.2 x 0.6 mm, 26 faces (baked)
FEATURE [App::Link] D9_LED_0603_1608Metric_691726ff2c38_ln_  label="D11_LED_0603_1608Metric_7ce10f24124e"
  LinkPlacement = pos=(140.35,-134.925,0) rot=(0,0,1;1.5708rad)
  LinkedObject = -> Shape012
  Placement = pos=(140.35,-134.925,0) rot=(0,0,1;1.5708rad)
FEATURE [App::Link] R11_R_0603_1608Metric_8d44d50ded66_ln_012  label="R21_R_0603_1608Metric_268238c76776"
  LinkPlacement = pos=(134.25,-112.75,0) rot=(0,0,1;3.14159rad)
  LinkedObject = -> Shape002
  Placement = pos=(134.25,-112.75,0) rot=(0,0,1;3.14159rad)
FEATURE [App::Link] R11_R_0603_1608Metric_8d44d50ded66_ln_013  label="R26_R_0603_1608Metric_3ef7509d2dfd"
  LinkPlacement = pos=(121.25,-132.5,0) rot=(0,0,1;3.14159rad)
  LinkedObject = -> Shape002
  Placement = pos=(121.25,-132.5,0) rot=(0,0,1;3.14159rad)
FEATURE [App::Link] C11_C_0603_1608Metric_b2591ca4353f_ln_016  label="C17_C_0603_1608Metric_872eda2552c1"
  LinkPlacement = pos=(134.5,-123.9,0) rot=(0,0,1;3.14159rad)
  LinkedObject = -> Shape
  Placement = pos=(134.5,-123.9,0) rot=(0,0,1;3.14159rad)
FEATURE [App::Link] D1_D_SMA_ee7b9d5fba9a_ln_003  label="D7_D_SMA_2ffd20934514"
  LinkPlacement = pos=(138.75,-139,0) rot=(0,0,1;3.14159rad)
  LinkedObject = -> Shape007
  Placement = pos=(138.75,-139,0) rot=(0,0,1;3.14159rad)
FEATURE [App::Link] C11_C_0603_1608Metric_b2591ca4353f_ln_017  label="C9_C_0603_1608Metric_5ca14c6f6c90"
  LinkPlacement = pos=(134.5,-125.45,0) rot=(0,0,1;3.14159rad)
  LinkedObject = -> Shape
  Placement = pos=(134.5,-125.45,0) rot=(0,0,1;3.14159rad)
FEATURE [App::Link] C11_C_0603_1608Metric_b2591ca4353f_ln_018  label="C18_C_0603_1608Metric_3f60591de45e"
  LinkPlacement = pos=(147.775,-123.81,0) rot=(0,0,1;0rad)
  LinkedObject = -> Shape
  Placement = pos=(147.775,-123.81,0) rot=(0,0,1;0rad)
FEATURE [App::Link] R11_R_0603_1608Metric_8d44d50ded66_ln_014  label="R28_R_0603_1608Metric_faebd804abb0"
  LinkPlacement = pos=(147.8,-122.25,0) rot=(0,0,1;3.14159rad)
  LinkedObject = -> Shape002
  Placement = pos=(147.8,-122.25,0) rot=(0,0,1;3.14159rad)
FEATURE [App::Link] D1_D_SMA_ee7b9d5fba9a_ln_004  label="D2_D_SMA_d4d7dce53c3e"
  LinkPlacement = pos=(120.5,-135.5,0) rot=(0,0,1;3.14159rad)
  LinkedObject = -> Shape007
  Placement = pos=(120.5,-135.5,0) rot=(0,0,1;3.14159rad)
FEATURE [App::Link] C11_C_0603_1608Metric_b2591ca4353f_ln_019  label="C7_C_0603_1608Metric_2c6dd344b303"
  LinkPlacement = pos=(151.25,-129.31,0) rot=(0,0,1;1.5708rad)
  LinkedObject = -> Shape
  Placement = pos=(151.25,-129.31,0) rot=(0,0,1;1.5708rad)
FEATURE [App::Link] R11_R_0603_1608Metric_8d44d50ded66_ln_015  label="R25_R_0603_1608Metric_f4cf285adc1c"
  LinkPlacement = pos=(154.5,-142.25,0) rot=(0,0,1;1.5708rad)
  LinkedObject = -> Shape002
  Placement = pos=(154.5,-142.25,0) rot=(0,0,1;1.5708rad)
FEATURE [App::Link] R11_R_0603_1608Metric_8d44d50ded66_ln_016  label="R24_R_0603_1608Metric_9c7afb44ef3d"
  LinkPlacement = pos=(138.6,-134.925,0) rot=(0,0,1;1.5708rad)
  LinkedObject = -> Shape002
  Placement = pos=(138.6,-134.925,0) rot=(0,0,1;1.5708rad)
FEATURE [App::Link] R11_R_0603_1608Metric_8d44d50ded66_ln_017  label="R19_R_0603_1608Metric_496b6ec453e1"
  LinkPlacement = pos=(134.5,-120.8,0) rot=(0,0,1;3.14159rad)
  LinkedObject = -> Shape002
  Placement = pos=(134.5,-120.8,0) rot=(0,0,1;3.14159rad)
FEATURE [App::Link] SW4_SW_SPST_TL3342_7108015214c8_ln_002  label="SW2_SW_SPST_TL3342_801a07d10ceb"
  LinkPlacement = pos=(119.25,-107,0) rot=(0,0,1;3.14159rad)
  LinkedObject = -> Shape011
  Placement = pos=(119.25,-107,0) rot=(0,0,1;3.14159rad)
FEATURE [App::Link] R11_R_0603_1608Metric_8d44d50ded66_ln_018  label="R30_R_0603_1608Metric_9b10f1c3a931"
  LinkPlacement = pos=(148.25,-134.75,0) rot=(0,0,1;0rad)
  LinkedObject = -> Shape002
  Placement = pos=(148.25,-134.75,0) rot=(0,0,1;0rad)
FEATURE [App::Link] D9_LED_0603_1608Metric_691726ff2c38_ln_001  label="D6_LED_0603_1608Metric_f1643554697a"
  LinkPlacement = pos=(137.25,-168.75,0) rot=(0,0,1;3.14159rad)
  LinkedObject = -> Shape012
  Placement = pos=(137.25,-168.75,0) rot=(0,0,1;3.14159rad)
FEATURE [App::Link] R11_R_0603_1608Metric_8d44d50ded66_ln_019  label="R16_R_0603_1608Metric_f548cd398350"
  LinkPlacement = pos=(125,-125.75,0) rot=(0,0,-1;1.5708rad)
  LinkedObject = -> Shape002
  Placement = pos=(125,-125.75,0) rot=(0,0,-1;1.5708rad)
FEATURE [Part::Feature] Shape015  label="U3_SOIJ_8_53x53mm_P127mm_a3aa00b83590[2]"
  Placement = pos=(129,-122.56,0) rot=(0,0,1;1.5708rad)
  shape: bbox 5.3 x 7.94 x 2.01 mm, 156 faces (baked)
FEATURE [App::Part] Top_a133
  Group = -> [Shape,Shape001,Shape002,C11_C_0603_1608Metric_b2591ca4353f_ln_,C11_C_0603_1608Metric_b2591ca4353f_ln_001,R11_R_0603_1608Metric_8d44d50ded66_ln_,Shape003,R11_R_0603_1608Metric_8d44d50ded66_ln_001,R11_R_0603_1608Metric_8d44d50ded66_ln_002,HRO_TYPE_C_31_M_12,C11_C_0603_1608Metric_b2591ca4353f_ln_002,R11_R_0603_1608Metric_8d44d50ded66_ln_003,U2_SOT_89_3_d67087812165_ln_,+62 more]
  Origin = -> Origin003
FEATURE [App::Part] Step_Models_a133
  Group = -> [Top_a133]
  Origin = -> Origin002
FEATURE [App::Part] Board_a133  label="MotorcycleBatterIsolator"
  Group = -> [Board_Geoms_a133,Step_Models_a133]
  Origin = -> Origin001
